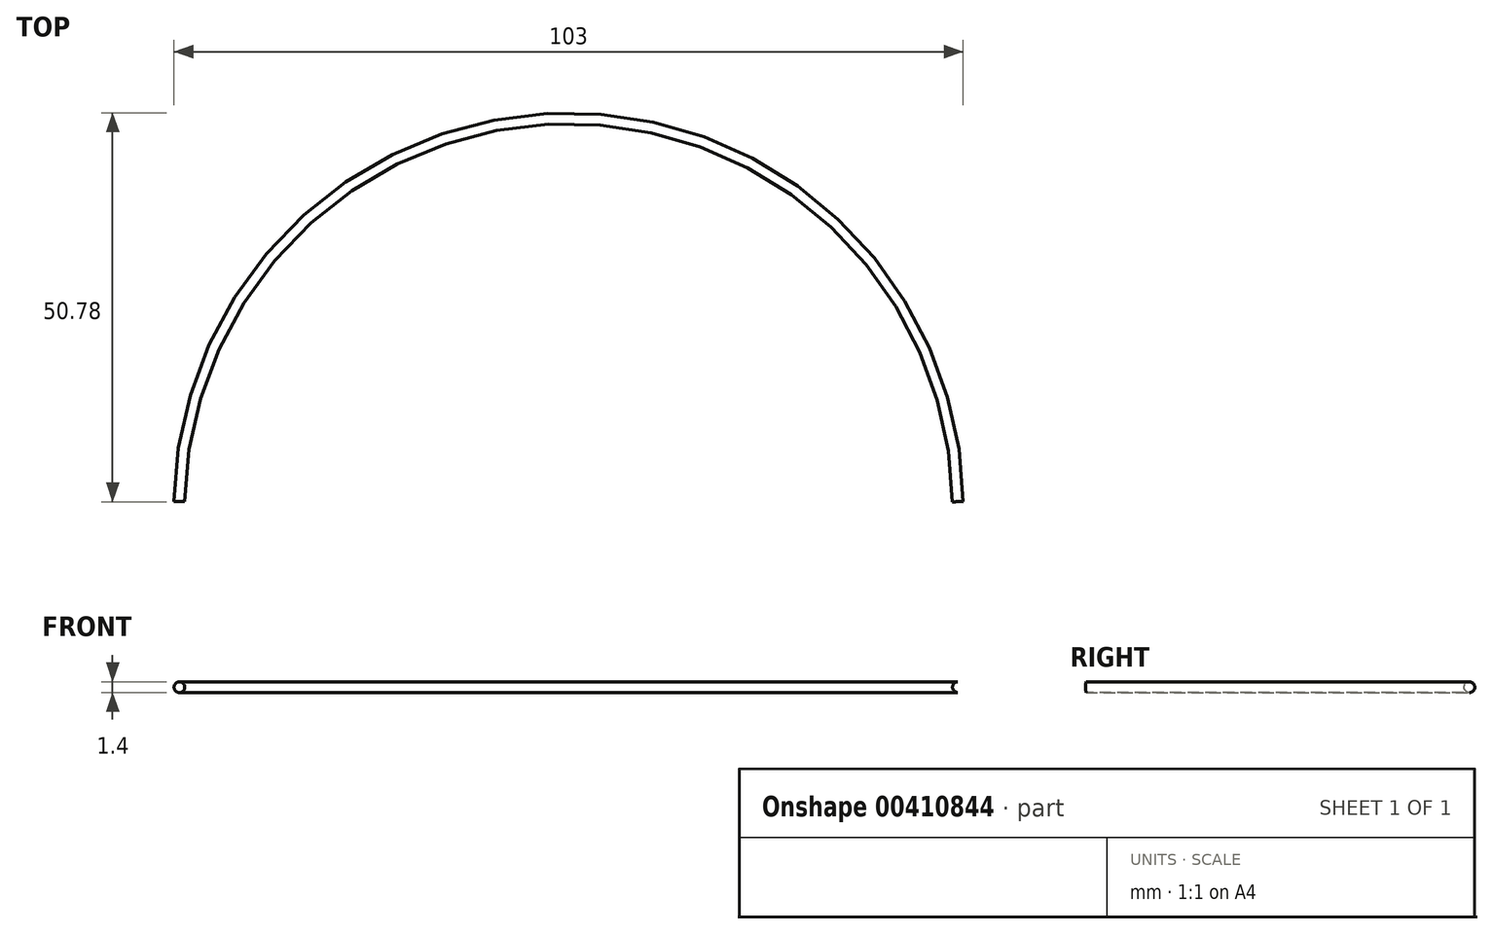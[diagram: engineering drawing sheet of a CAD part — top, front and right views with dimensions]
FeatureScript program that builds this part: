
annotation { "Feature Type Name" : "Feature", "Feature Type Description" : "" }
export const myFeature = defineFeature(function(context is Context, id is Id, definition is map)
    precondition{}
    {
        {
            var Q0;
            Q0=qCreatedBy(makeId("Top.planeOp"),FACE);
            var sketch = newSketch(context, id + "F0", { "sketchPlane" : qUnion([Q0])});
            skArc(sketch, "E0", {"start": v(50.8, 0) * mm, "mid": v(0, 50.05) * mm, "end": v(-50.8, 0) * mm});
            skSolve(sketch);
        }
        {
            var Q0;
            Q0=qCreatedBy(makeId("Front.planeOp"),FACE);
            var sketch = newSketch(context, id + "F1", { "sketchPlane" : qUnion([Q0])});
            skCircle(sketch, "E1", {"center": v(-50.8, 0) * mm, "radius": 0.7 * mm});
            skSolve(sketch);
        }
        {
            var Q0;
            Q0=makeQuery(id+"F1.imprint","IMPRINT",FACE,{"disambiguationData":[TD([[makeQuery(id+"F1.imprint","IMPRINT",EDGE,{"derivedFrom":sQuery(id+"F1.wireOp",EDGE,"E1")}),1.0]])]});
            var Q1;
            Q1=sQuery(id+"F1.wireOp",EDGE,"E1");
            var Q2;
            Q2=sQuery(id+"F0.wireOp",EDGE,"E0");
            sweep(context, id + "F2", {"profiles" : qUnion([Q0]), "surfaceProfiles" : qUnion([Q1]), "path" : qUnion([Q2])});
        }
    });
